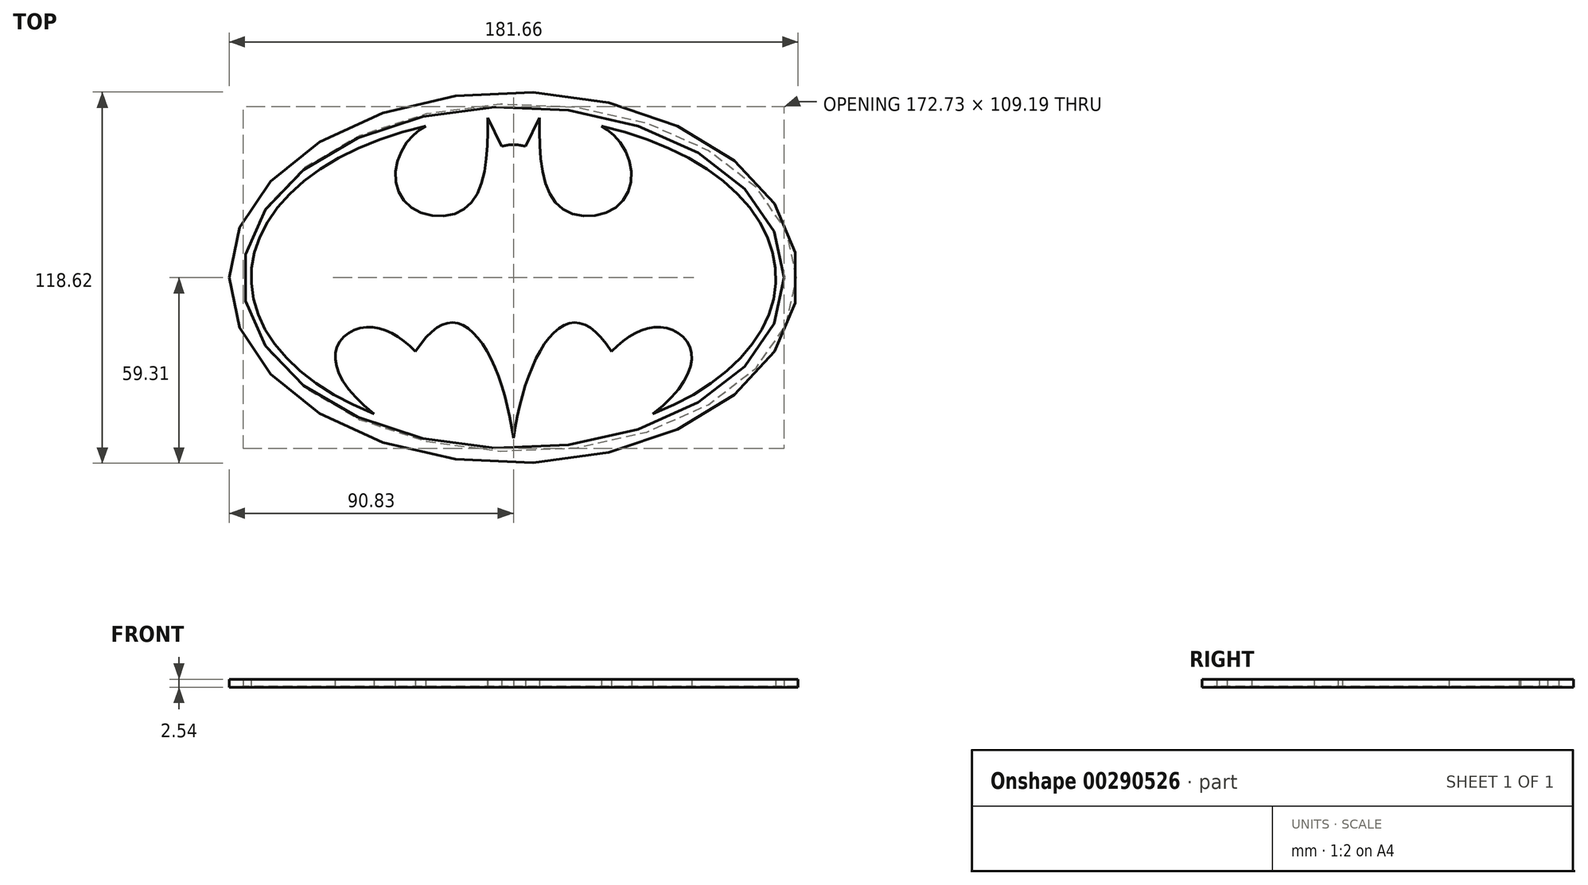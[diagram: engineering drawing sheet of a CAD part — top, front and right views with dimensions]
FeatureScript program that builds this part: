
annotation { "Feature Type Name" : "Feature", "Feature Type Description" : "" }
export const myFeature = defineFeature(function(context is Context, id is Id, definition is map)
    precondition{}
    {
        {
            var Q0;
            Q0=qCreatedBy(makeId("Top.planeOp"),FACE);
            var sketch = newSketch(context, id + "F0", { "sketchPlane" : qUnion([Q0])});
            skEllipse(sketch, "E0", {"center": v(0, 0) * mm, "majorRadius": 90.83 * mm, "minorRadius": 59.3 * mm, "majorAxis": v(-1, 0)});
            skEllipse(sketch, "E1", {"center": v(0, 0) * mm, "majorRadius": 86.36 * mm, "minorRadius": 54.6 * mm, "majorAxis": v(1, 0)});
            skSolve(sketch);
        }
        {
            var Q0;
            Q0 = qSketchRegion(id + "F0", true);
            extrude(context, id + "F1", {"entities" : qUnion([Q0]), "depth" : 2.54 * mm});
        }
        {
            var Q0;
            Q0=qCreatedBy(makeId("Top.planeOp"),FACE);
            var sketch = newSketch(context, id + "F2", { "sketchPlane" : qUnion([Q0])});
            skEllipse(sketch, "E2", {"center": v(1.88, 0) * mm, "majorRadius": 88.48 * mm, "minorRadius": 55.55 * mm, "majorAxis": v(1, 0)});
            skSolve(sketch);
        }
        {
            var Q0;
            Q0 = qSketchRegion(id + "F2", true);
            extrude(context, id + "F3", {"entities" : qUnion([Q0]), "depth" : 0.25 * mm});
        }
        {
            var Q0;
            Q0=qCreatedBy(makeId("Top.planeOp"),FACE);
            var sketch = newSketch(context, id + "F4", { "sketchPlane" : qUnion([Q0])});
            skEllipticalArc(sketch, "E3", {});
            skPoint(sketch, "E4.visualSharp", {"position": v(-11.66, 24.93) * mm});
            skFitSpline(sketch, "E5", {"points": [v(-28.04, 48.36) * mm, v(-34.2, 43.01) * mm, v(-37.64, 31.23) * mm, v(-31.4, 21.59) * mm, v(-17.5, 20.9) * mm, v(-10.02, 30.8) * mm, v(-8.28, 51.07) * mm], "startDerivative": vector(-37.53, -17.95) * mm, "endDerivative": vector(-0.4, 101.09) * mm});
            skLineSegment(sketch, "E6", {"start": v(0, 41.94) * mm, "end": v(0, 0) * mm, "construction": true});
            skFitSpline(sketch, "E7.MirrorCS", {"points": [v(28.04, 48.36) * mm, v(34.2, 43.01) * mm, v(37.64, 31.23) * mm, v(31.4, 21.59) * mm, v(17.5, 20.9) * mm, v(10.02, 30.8) * mm, v(8.28, 51.07) * mm], "startDerivative": vector(37.53, -17.95) * mm, "endDerivative": vector(0.4, 101.09) * mm});
            skLineSegment(sketch, "E8", {"start": v(-8.28, 51.07) * mm, "end": v(-3.8, 41.94) * mm});
            skPoint(sketch, "E9.orphan", {"position": v(0, 51.32) * mm});
            skLineSegment(sketch, "E10.MirrorCS", {"start": v(8.28, 51.07) * mm, "end": v(3.8, 41.94) * mm});
            skFitSpline(sketch, "E11", {"points": [v(-3.8, 41.94) * mm, v(0, 42.5) * mm, v(3.8, 41.94) * mm], "startDerivative": vector(7.62, 1.72) * mm, "endDerivative": vector(7.62, -1.72) * mm});
            skFitSpline(sketch, "E12", {"points": [v(0, -51.32) * mm, v(-9.88, -21.18) * mm, v(-19.77, -14.35) * mm, v(-31.3, -23.53) * mm], "startDerivative": vector(-11.42, 79.44) * mm, "endDerivative": vector(-39.53, -59.3) * mm});
            skFitSpline(sketch, "E13", {"points": [v(-31.3, -23.53) * mm, v(-45.89, -15.77) * mm, v(-56.24, -21.89) * mm, v(-44.52, -43.47) * mm], "startDerivative": vector(-41.2, 39.84) * mm, "endDerivative": vector(79.75, -60.01) * mm});
            skLineSegment(sketch, "E14", {"start": v(0, -51.32) * mm, "end": v(0, 0) * mm, "construction": true});
            skFitSpline(sketch, "E15.MirrorCS", {"points": [v(0, -51.32) * mm, v(9.88, -21.18) * mm, v(19.77, -14.35) * mm, v(31.3, -23.53) * mm], "startDerivative": vector(11.42, 79.44) * mm, "endDerivative": vector(39.53, -59.3) * mm});
            skFitSpline(sketch, "E16.MirrorCS", {"points": [v(31.3, -23.53) * mm, v(45.89, -15.77) * mm, v(56.24, -21.89) * mm, v(44.52, -43.47) * mm], "startDerivative": vector(41.2, 39.84) * mm, "endDerivative": vector(-79.75, -60.01) * mm});
            skEllipticalArc(sketch, "E17.trimOffspring", {});
            const initialGuessF4  = {"E3": [0, 0, -1, 0, 0.08377639440239934, 0.05131702398586518, 5.0536322319070806, 1.0105696278196472], "E17.trimOffspring": [0, 0, -1, 0, 0.08377639440239934, 0.05131702398586518, 2.131023025770146, 4.3711457288623]};
            skSetInitialGuess(sketch, initialGuessF4);
            skSolve(sketch);
        }
        {
            var Q0;
            Q0 = qSketchRegion(id + "F4", true);
            extrude(context, id + "F5", {"entities" : qUnion([Q0]), "depth" : 2.54 * mm});
        }
    });
